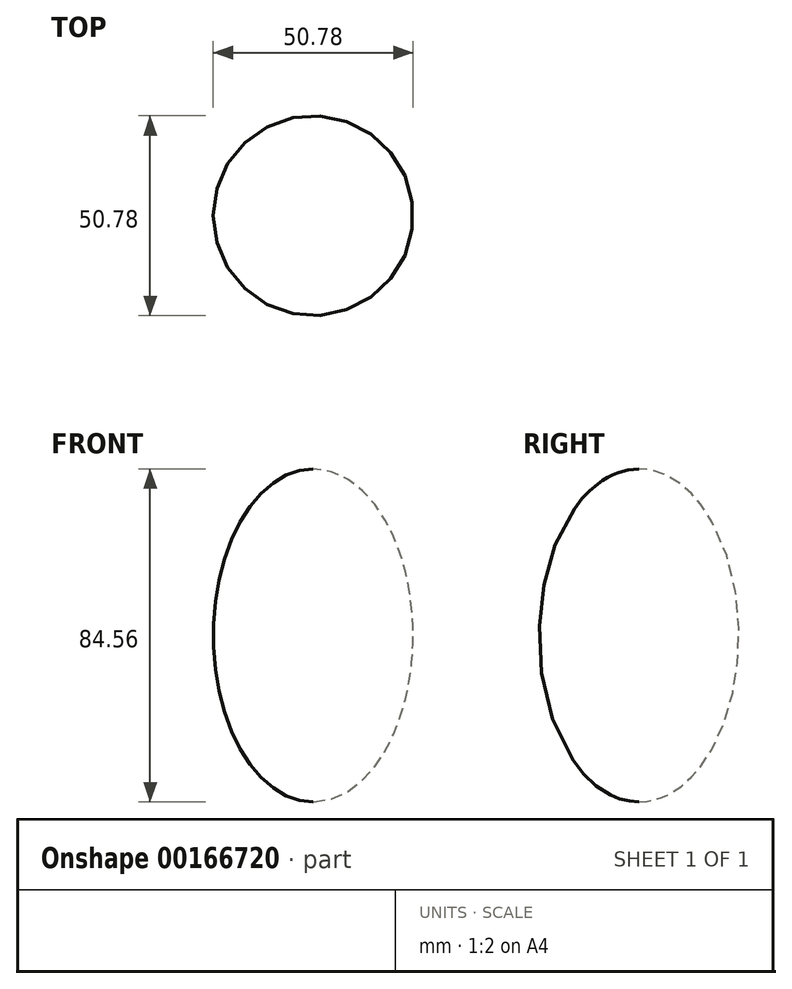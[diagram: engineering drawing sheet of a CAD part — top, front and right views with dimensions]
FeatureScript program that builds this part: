
annotation { "Feature Type Name" : "Feature", "Feature Type Description" : "" }
export const myFeature = defineFeature(function(context is Context, id is Id, definition is map)
    precondition{}
    {
        {
            var Q0;
            Q0=qCreatedBy(makeId("Front.planeOp"),FACE);
            var sketch = newSketch(context, id + "F0", { "sketchPlane" : qUnion([Q0])});
            skEllipse(sketch, "E0", {"center": v(0, 0) * mm, "majorRadius": 42.28 * mm, "minorRadius": 25.39 * mm, "majorAxis": v(0, 1)});
            skLineSegment(sketch, "E1", {"start": v(0, 42.28) * mm, "end": v(0, -42.28) * mm});
            skSolve(sketch);
        }
        {
            var Q0;
            {var subQ0=sQuery(id+"F0.wireOp",EDGE,"E1");Q0=makeQuery(id+"F0.imprint","IMPRINT",FACE,{"disambiguationData":[TD([[makeQuery(id+"F0.imprint","IMPRINT",EDGE,{"derivedFrom":subQ0}),-1.0]])]});}
            var Q1;
            Q1=sQuery(id+"F0.wireOp",EDGE,"E1");
            revolve(context, id + "F1", {"entities" : qUnion([Q0]), "axis" : qUnion([Q1]), "revolveType" : RevolveType.FULL});
        }
    });
